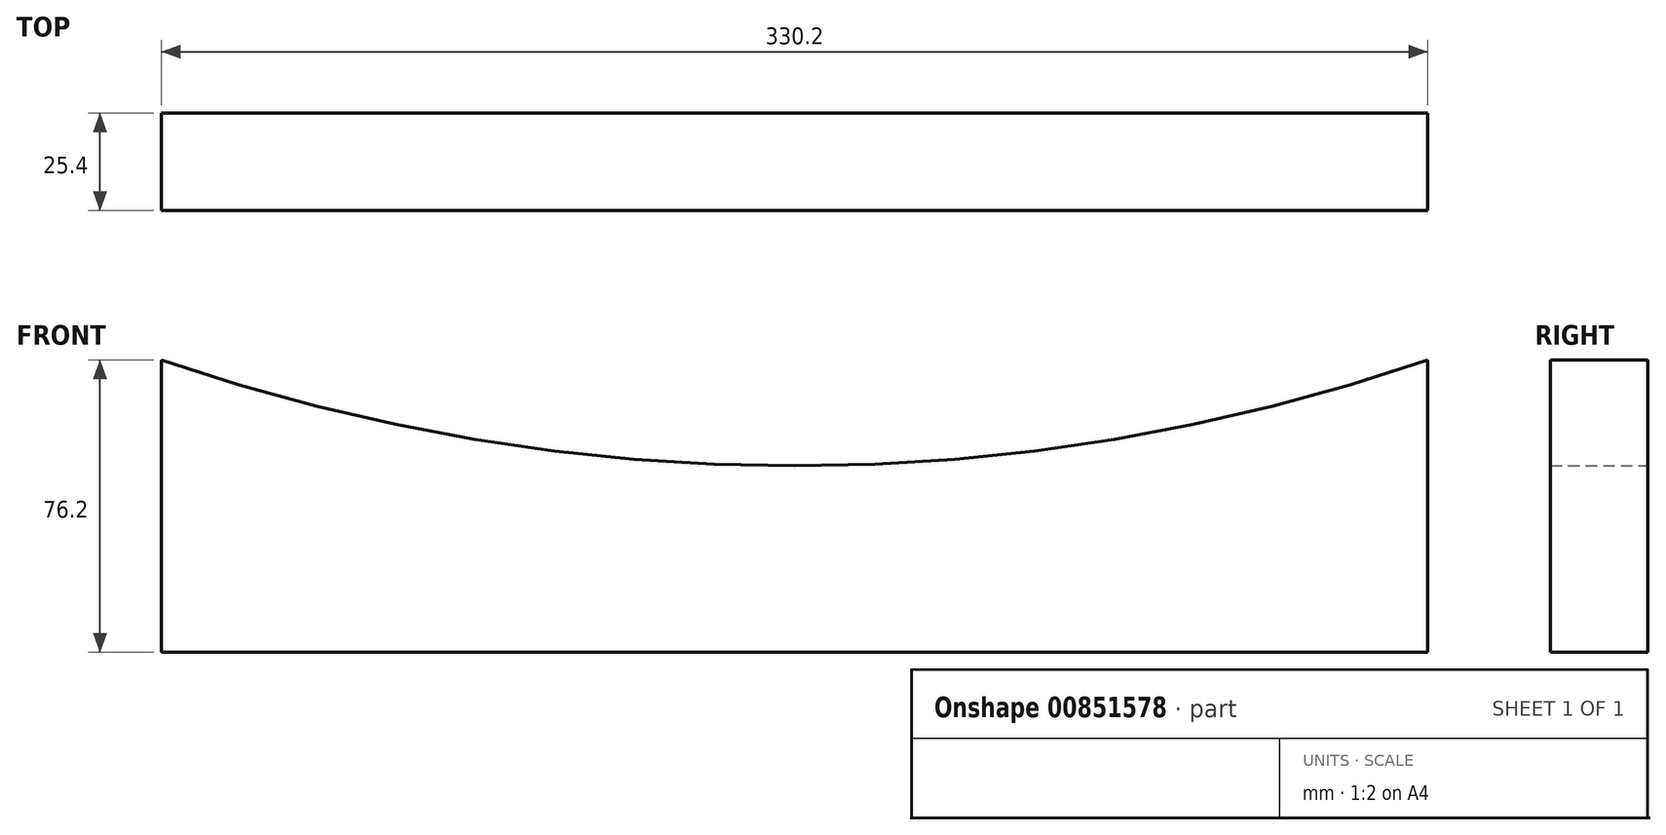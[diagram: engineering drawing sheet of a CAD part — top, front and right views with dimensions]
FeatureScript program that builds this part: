
annotation { "Feature Type Name" : "Feature", "Feature Type Description" : "" }
export const myFeature = defineFeature(function(context is Context, id is Id, definition is map)
    precondition{}
    {
        {
            var Q0;
            Q0=qCreatedBy(makeId("Front.planeOp"),FACE);
            var sketch = newSketch(context, id + "F0", { "sketchPlane" : qUnion([Q0])});
            skLineSegment(sketch, "E0.top", {"start": v(-137.4, -26.95) * mm, "end": v(192.8, -26.95) * mm});
            skLineSegment(sketch, "E0.left", {"start": v(-137.4, 49.25) * mm, "end": v(-137.4, -26.95) * mm});
            skLineSegment(sketch, "E0.right", {"start": v(192.8, 49.25) * mm, "end": v(192.8, -26.95) * mm});
            skArc(sketch, "E1", {"start": v(-137.4, 49.25) * mm, "mid": v(27.7, 21.67) * mm, "end": v(192.8, 49.25) * mm});
            skSolve(sketch);
        }
        {
            var Q0;
            Q0 = qSketchRegion(id + "F0", true);
            extrude(context, id + "F1", {"entities" : qUnion([Q0]), "depth" : 25.4 * mm, "offsetDistance" : 25.4 * mm});
        }
    });
